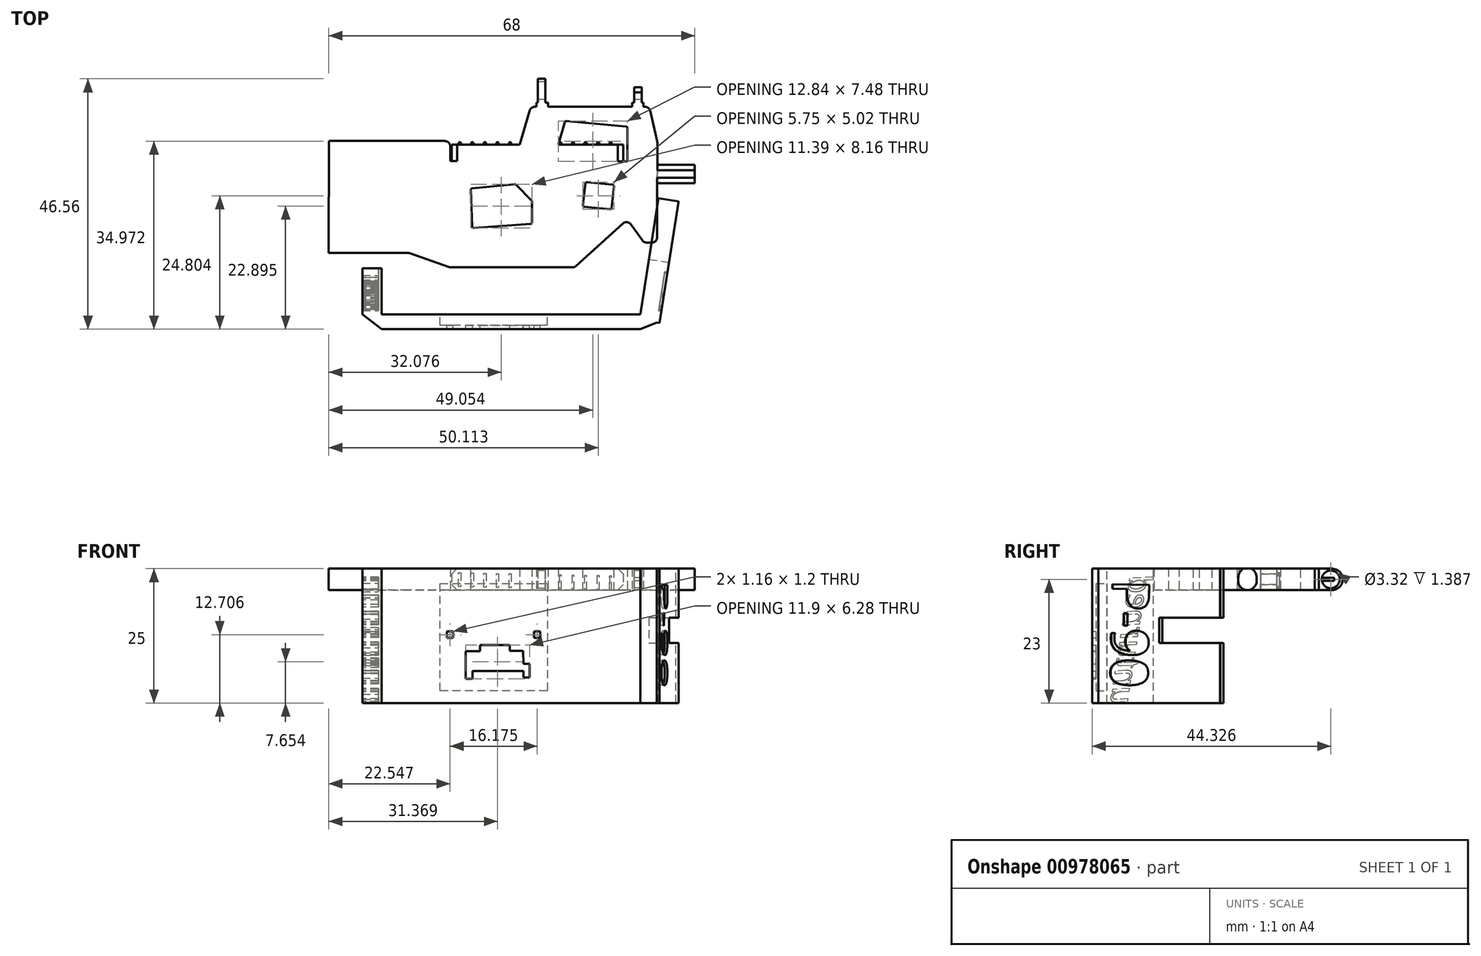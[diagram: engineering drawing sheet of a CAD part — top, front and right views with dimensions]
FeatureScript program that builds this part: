
annotation { "Feature Type Name" : "Feature", "Feature Type Description" : "" }
export const myFeature = defineFeature(function(context is Context, id is Id, definition is map)
    precondition{}
    {
        {
            var Q0;
            Q0=qCreatedBy(makeId("Top.planeOp"),FACE);
            var sketch = newSketch(context, id + "F0", { "sketchPlane" : qUnion([Q0])});
            skLineSegment(sketch, "E0", {"start": v(-19.87, -5.27) * mm, "end": v(2.7, -5.27) * mm});
            skLineSegment(sketch, "E1", {"start": v(2.7, -5.27) * mm, "end": v(2.7, -8.97) * mm});
            skLineSegment(sketch, "E2", {"start": v(2.7, -8.97) * mm, "end": v(14.76, -8.97) * mm});
            skLineSegment(sketch, "E3", {"start": v(14.76, -8.97) * mm, "end": v(17.64, 1.08) * mm});
            skLineSegment(sketch, "E4", {"start": v(17.64, 1.08) * mm, "end": v(18.71, 1.08) * mm});
            skLineSegment(sketch, "E5", {"start": v(18.71, 1.08) * mm, "end": v(18.71, 1.84) * mm});
            skLineSegment(sketch, "E6", {"start": v(18.71, 1.84) * mm, "end": v(18.98, 1.84) * mm});
            skLineSegment(sketch, "E7", {"start": v(18.98, 1.84) * mm, "end": v(18.98, 6.3) * mm});
            skLineSegment(sketch, "E8", {"start": v(18.98, 6.3) * mm, "end": v(20.34, 6.3) * mm});
            skLineSegment(sketch, "E9", {"start": v(20.34, 6.3) * mm, "end": v(20.37, 1.84) * mm});
            skLineSegment(sketch, "E10", {"start": v(20.37, 1.84) * mm, "end": v(20.86, 1.84) * mm});
            skLineSegment(sketch, "E11", {"start": v(20.86, 1.84) * mm, "end": v(20.86, 1.1) * mm});
            skLineSegment(sketch, "E12", {"start": v(20.86, 1.1) * mm, "end": v(36.46, 1.1) * mm});
            skLineSegment(sketch, "E13", {"start": v(36.46, 1.1) * mm, "end": v(36.46, 1.84) * mm});
            skLineSegment(sketch, "E14", {"start": v(36.46, 1.84) * mm, "end": v(36.87, 1.84) * mm});
            skLineSegment(sketch, "E15", {"start": v(36.87, 1.84) * mm, "end": v(36.87, 3.78) * mm});
            skLineSegment(sketch, "E16", {"start": v(36.87, 3.78) * mm, "end": v(38.25, 3.78) * mm});
            skLineSegment(sketch, "E17", {"start": v(38.25, 3.78) * mm, "end": v(38.25, 1.84) * mm});
            skLineSegment(sketch, "E18", {"start": v(38.25, 1.84) * mm, "end": v(38.6, 1.84) * mm});
            skLineSegment(sketch, "E19", {"start": v(38.6, 1.84) * mm, "end": v(38.6, 1.1) * mm});
            skLineSegment(sketch, "E20", {"start": v(38.6, 1.1) * mm, "end": v(39.64, 1.1) * mm});
            skLineSegment(sketch, "E21", {"start": v(39.64, 1.1) * mm, "end": v(41.15, -5.34) * mm});
            skLineSegment(sketch, "E22", {"start": v(41.15, -5.34) * mm, "end": v(41.15, -9.7) * mm});
            skLineSegment(sketch, "E23", {"start": v(41.15, -9.7) * mm, "end": v(48.11, -9.7) * mm});
            skLineSegment(sketch, "E24", {"start": v(48.11, -9.7) * mm, "end": v(48.11, -13.13) * mm});
            skLineSegment(sketch, "E25", {"start": v(48.11, -13.13) * mm, "end": v(41.14, -13.13) * mm});
            skLineSegment(sketch, "E26", {"start": v(41.14, -13.13) * mm, "end": v(41.14, -24.16) * mm});
            skLineSegment(sketch, "E27", {"start": v(41.14, -24.16) * mm, "end": v(38.66, -24.16) * mm});
            skLineSegment(sketch, "E28", {"start": v(38.66, -24.16) * mm, "end": v(35.58, -19.85) * mm});
            skLineSegment(sketch, "E29", {"start": v(35.58, -19.85) * mm, "end": v(25.77, -28.76) * mm});
            skLineSegment(sketch, "E30", {"start": v(25.77, -28.76) * mm, "end": v(2.57, -28.76) * mm});
            skLineSegment(sketch, "E31", {"start": v(2.57, -28.76) * mm, "end": v(-4.99, -26.08) * mm});
            skLineSegment(sketch, "E32", {"start": v(-4.99, -26.08) * mm, "end": v(-19.89, -26.08) * mm});
            skLineSegment(sketch, "E33", {"start": v(-19.89, -26.08) * mm, "end": v(-19.87, -5.27) * mm});
            skLineSegment(sketch, "E34", {"start": v(2.96, -5.97) * mm, "end": v(2.96, -8.97) * mm});
            skLineSegment(sketch, "E35", {"start": v(2.96, -5.97) * mm, "end": v(15.62, -5.97) * mm});
            skLineSegment(sketch, "E36", {"start": v(22.62, -5.96) * mm, "end": v(34.83, -5.96) * mm});
            skLineSegment(sketch, "E37", {"start": v(34.83, -5.96) * mm, "end": v(34.83, -9.03) * mm});
            skLineSegment(sketch, "E38", {"start": v(34.83, -9.03) * mm, "end": v(21.86, -9.03) * mm});
            skLineSegment(sketch, "E39", {"start": v(21.86, -9.03) * mm, "end": v(24.02, -1.53) * mm});
            skLineSegment(sketch, "E40", {"start": v(24.02, -1.53) * mm, "end": v(35.58, -2.57) * mm});
            skLineSegment(sketch, "E41", {"start": v(35.58, -2.57) * mm, "end": v(35.58, -9.03) * mm});
            skLineSegment(sketch, "E42", {"start": v(35.58, -9.03) * mm, "end": v(34.83, -9.03) * mm});
            skLineSegment(sketch, "E43", {"start": v(27.78, -12.92) * mm, "end": v(27.32, -17.45) * mm});
            skLineSegment(sketch, "E44", {"start": v(27.32, -17.45) * mm, "end": v(32.66, -18) * mm});
            skLineSegment(sketch, "E45", {"start": v(32.66, -18) * mm, "end": v(33.13, -13.41) * mm});
            skLineSegment(sketch, "E46", {"start": v(33.13, -13.41) * mm, "end": v(27.78, -12.92) * mm});
            skLineSegment(sketch, "E47", {"start": v(14.8, -13.27) * mm, "end": v(17.88, -16.43) * mm});
            skLineSegment(sketch, "E48", {"start": v(17.88, -16.43) * mm, "end": v(17.88, -20.66) * mm});
            skLineSegment(sketch, "E49", {"start": v(17.88, -20.66) * mm, "end": v(6.8, -21.47) * mm});
            skLineSegment(sketch, "E50", {"start": v(6.8, -21.47) * mm, "end": v(6.48, -14.11) * mm});
            skLineSegment(sketch, "E51", {"start": v(6.48, -14.11) * mm, "end": v(14.8, -13.27) * mm});
            skSolve(sketch);
        }
        {
            var Q0;
            Q0=makeQuery(id+"F0.imprint","IMPRINT",FACE,{"disambiguationData":[TD([[makeQuery(id+"F0.imprint","IMPRINT",EDGE,{"derivedFrom":sQuery(id+"F0.wireOp",EDGE,"E0")}),-1.0]])]});
            var Q1;
            {var subQ3=sQuery(id+"F0.wireOp",EDGE,"E34");Q1=makeQuery(id+"F0.imprint","IMPRINT",FACE,{"disambiguationData":[TD([[makeQuery(id+"F0.imprint","IMPRINT",EDGE,{"derivedFrom":subQ3}),1.0]])]});}
            var Q2;
            {var subQ0=sQuery(id+"F0.wireOp",EDGE,"E37");Q2=makeQuery(id+"F0.imprint","IMPRINT",FACE,{"disambiguationData":[TD([[makeQuery(id+"F0.imprint","IMPRINT",EDGE,{"derivedFrom":subQ0}),-1.0]])]});}
            extrude(context, id + "F1", {"entities" : qUnion([Q0, Q1, Q2]), "depth" : 4 * mm, "offsetDistance" : 25.4 * mm});
        }
        {
            var Q0;
            Q0=makeQuery(id+"F1.opExtrude","SWEPT_FACE",FACE,{"disambiguationData":[OSD([sQuery(id+"F0.wireOp",EDGE,"E7")])]});
            var sketch = newSketch(context, id + "F2", { "sketchPlane" : qUnion([Q0])});
            skLineSegment(sketch, "E52", {"start": v(-6.3, 0) * mm, "end": v(-1.84, 4) * mm});
            skLineSegment(sketch, "E53", {"start": v(-6.3, 4) * mm, "end": v(-1.84, 0) * mm});
            skCircle(sketch, "E54", {"center": v(-4.07, 2) * mm, "radius": 1.66 * mm});
            skSolve(sketch);
        }
        {
            var Q0;
            Q0 = qSketchRegion(id + "F2", true);
            extrude(context, id + "F3", {"entities" : qUnion([Q0]), "operationType" : NewBodyOperationType.REMOVE, "oppositeDirection" : true, "depth" : 25 * mm, "offsetDistance" : 25 * mm});
        }
        {
            var Q0;
            Q0=makeQuery(id+"F1.opExtrude","CAP_EDGE",EDGE,{"disambiguationData":[OSD([sQuery(id+"F0.wireOp",EDGE,"E23")])],"isStart":false});
            var Q1;
            Q1=makeQuery(id+"F1.opExtrude","CAP_EDGE",EDGE,{"disambiguationData":[OSD([sQuery(id+"F0.wireOp",EDGE,"E23")])],"isStart":true});
            var Q2;
            Q2=makeQuery(id+"F1.opExtrude","CAP_EDGE",EDGE,{"disambiguationData":[OSD([sQuery(id+"F0.wireOp",EDGE,"E25")])],"isStart":false});
            var Q3;
            Q3=makeQuery(id+"F1.opExtrude","CAP_EDGE",EDGE,{"disambiguationData":[OSD([sQuery(id+"F0.wireOp",EDGE,"E25")])],"isStart":true});
            fillet(context, id + "F4", {"entities" : qUnion([Q0, Q1, Q2, Q3]), "radius" : 1.7 * mm, "tangentPropagation" : true, "allowEdgeOverflow" : false});
        }
        {
            var Q0;
            Q0=makeQuery(id+"F1.opExtrude","CAP_EDGE",EDGE,{"disambiguationData":[OSD([sQuery(id+"F0.wireOp",EDGE,"E34")])],"isStart":false});
            var Q1;
            Q1=makeQuery(id+"F1.opExtrude","CAP_EDGE",EDGE,{"disambiguationData":[OSD([sQuery(id+"F0.wireOp",EDGE,"E34")])],"isStart":true});
            var Q2;
            Q2=makeQuery(id+"F1.opExtrude","CAP_EDGE",EDGE,{"disambiguationData":[OSD([sQuery(id+"F0.wireOp",EDGE,"E37")])],"isStart":false});
            var Q3;
            Q3=makeQuery(id+"F1.opExtrude","CAP_EDGE",EDGE,{"disambiguationData":[OSD([sQuery(id+"F0.wireOp",EDGE,"E37")])],"isStart":true});
            chamfer(context, id + "F5", {"entities" : qUnion([Q0, Q1, Q2, Q3]), "width" : 1 * mm, "tangentPropagation" : true});
        }
        {
            var Q0;
            Q0=makeQuery(id+"F1.opExtrude","CAP_FACE",FACE,{"disambiguationData":[OSD([sQuery(id+"F0.wireOp",EDGE,"E0"),sQuery(id+"F0.wireOp",EDGE,"E1"),sQuery(id+"F0.wireOp",EDGE,"E2"),sQuery(id+"F0.wireOp",EDGE,"E3"),sQuery(id+"F0.wireOp",EDGE,"E4"),sQuery(id+"F0.wireOp",EDGE,"E5"),sQuery(id+"F0.wireOp",EDGE,"E6"),sQuery(id+"F0.wireOp",EDGE,"E7"),sQuery(id+"F0.wireOp",EDGE,"E8"),sQuery(id+"F0.wireOp",EDGE,"E9"),sQuery(id+"F0.wireOp",EDGE,"E10"),sQuery(id+"F0.wireOp",EDGE,"E11"),sQuery(id+"F0.wireOp",EDGE,"E12"),sQuery(id+"F0.wireOp",EDGE,"E13"),sQuery(id+"F0.wireOp",EDGE,"E14"),sQuery(id+"F0.wireOp",EDGE,"E15"),sQuery(id+"F0.wireOp",EDGE,"E16"),sQuery(id+"F0.wireOp",EDGE,"E17"),sQuery(id+"F0.wireOp",EDGE,"E18"),sQuery(id+"F0.wireOp",EDGE,"E19"),sQuery(id+"F0.wireOp",EDGE,"E20"),sQuery(id+"F0.wireOp",EDGE,"E21"),sQuery(id+"F0.wireOp",EDGE,"E22"),sQuery(id+"F0.wireOp",EDGE,"E23"),sQuery(id+"F0.wireOp",EDGE,"E24"),sQuery(id+"F0.wireOp",EDGE,"E25"),sQuery(id+"F0.wireOp",EDGE,"E26"),sQuery(id+"F0.wireOp",EDGE,"E27"),sQuery(id+"F0.wireOp",EDGE,"E28"),sQuery(id+"F0.wireOp",EDGE,"E29"),sQuery(id+"F0.wireOp",EDGE,"E30"),sQuery(id+"F0.wireOp",EDGE,"E31"),sQuery(id+"F0.wireOp",EDGE,"E32"),sQuery(id+"F0.wireOp",EDGE,"E33"),sQuery(id+"F0.wireOp",EDGE,"E34"),sQuery(id+"F0.wireOp",EDGE,"E35"),sQuery(id+"F0.wireOp",EDGE,"E36"),sQuery(id+"F0.wireOp",EDGE,"E37"),sQuery(id+"F0.wireOp",EDGE,"E39"),sQuery(id+"F0.wireOp",EDGE,"E40"),sQuery(id+"F0.wireOp",EDGE,"E41"),sQuery(id+"F0.wireOp",EDGE,"E42"),sQuery(id+"F0.wireOp",EDGE,"E43"),sQuery(id+"F0.wireOp",EDGE,"E44"),sQuery(id+"F0.wireOp",EDGE,"E45"),sQuery(id+"F0.wireOp",EDGE,"E46"),sQuery(id+"F0.wireOp",EDGE,"E47"),sQuery(id+"F0.wireOp",EDGE,"E48"),sQuery(id+"F0.wireOp",EDGE,"E49"),sQuery(id+"F0.wireOp",EDGE,"E50"),sQuery(id+"F0.wireOp",EDGE,"E51")])],"isStart":false});
            var sketch = newSketch(context, id + "F6", { "sketchPlane" : qUnion([Q0])});
            skLineSegment(sketch, "E55", {"start": v(3.96, -8.97) * mm, "end": v(33.83, -9.03) * mm});
            skSolve(sketch);
        }
        {
            var Q0;
            Q0=makeQuery(id+"F1.opExtrude","SWEPT_EDGE",EDGE,{"disambiguationData":[OSD([sQuery(id+"F0.wireOp",EDGE,"E31"),sQuery(id+"F0.wireOp",EDGE,"E32")])]});
            var Q1;
            Q1=makeQuery(id+"F1.opExtrude","SWEPT_EDGE",EDGE,{"disambiguationData":[OSD([sQuery(id+"F0.wireOp",EDGE,"E30"),sQuery(id+"F0.wireOp",EDGE,"E31")])]});
            var Q2;
            Q2=makeQuery(id+"F1.opExtrude","SWEPT_EDGE",EDGE,{"disambiguationData":[OSD([sQuery(id+"F0.wireOp",EDGE,"E29"),sQuery(id+"F0.wireOp",EDGE,"E30")])]});
            var Q3;
            Q3=makeQuery(id+"F1.opExtrude","SWEPT_EDGE",EDGE,{"disambiguationData":[OSD([sQuery(id+"F0.wireOp",EDGE,"E28"),sQuery(id+"F0.wireOp",EDGE,"E29")])]});
            var Q4;
            Q4=makeQuery(id+"F1.opExtrude","SWEPT_EDGE",EDGE,{"disambiguationData":[OSD([sQuery(id+"F0.wireOp",EDGE,"E27"),sQuery(id+"F0.wireOp",EDGE,"E28")])]});
            var Q5;
            Q5=makeQuery(id+"F1.opExtrude","SWEPT_EDGE",EDGE,{"disambiguationData":[OSD([sQuery(id+"F0.wireOp",EDGE,"E26"),sQuery(id+"F0.wireOp",EDGE,"E27")])]});
            var Q6;
            Q6=makeQuery(id+"F1.opExtrude","SWEPT_EDGE",EDGE,{"disambiguationData":[OSD([sQuery(id+"F0.wireOp",EDGE,"E21"),sQuery(id+"F0.wireOp",EDGE,"E22")])]});
            var Q7;
            Q7=makeQuery(id+"F1.opExtrude","SWEPT_EDGE",EDGE,{"disambiguationData":[OSD([sQuery(id+"F0.wireOp",EDGE,"E20"),sQuery(id+"F0.wireOp",EDGE,"E21")])]});
            var Q8;
            Q8=makeQuery(id+"F1.opExtrude","SWEPT_EDGE",EDGE,{"disambiguationData":[OSD([sQuery(id+"F0.wireOp",EDGE,"E3"),sQuery(id+"F0.wireOp",EDGE,"E4")])]});
            var Q9;
            Q9=makeQuery(id+"F1.opExtrude","SWEPT_EDGE",EDGE,{"disambiguationData":[OSD([sQuery(id+"F0.wireOp",EDGE,"E0"),sQuery(id+"F0.wireOp",EDGE,"E1")])]});
            fillet(context, id + "F7", {"entities" : qUnion([Q0, Q1, Q2, Q3, Q4, Q5, Q6, Q7, Q8, Q9]), "radius" : 1 * mm, "tangentPropagation" : true, "allowEdgeOverflow" : false});
        }
        {
            var Q0;
            Q0=makeQuery(id+"F1.opExtrude","SWEPT_FACE",FACE,{"disambiguationData":[OSD([sQuery(id+"F0.wireOp",EDGE,"E35")])]});
            var sketch = newSketch(context, id + "F8", { "sketchPlane" : qUnion([Q0])});
            skLineSegment(sketch, "E56", {"start": v(-4.25, 0.64) * mm, "end": v(-4.25, 3.24) * mm});
            skLineSegment(sketch, "E57", {"start": v(-4.25, 3.24) * mm, "end": v(-4.66, 3.24) * mm});
            skLineSegment(sketch, "E58", {"start": v(-4.66, 3.24) * mm, "end": v(-4.66, 0.65) * mm});
            skLineSegment(sketch, "E59", {"start": v(-4.66, 0.65) * mm, "end": v(-4.25, 0.64) * mm});
            skLineSegment(sketch, "E60.1.0.0", {"start": v(-6.59, 0.59) * mm, "end": v(-6.59, 3.2) * mm});
            skLineSegment(sketch, "E60.1.0.1", {"start": v(-7, 3.2) * mm, "end": v(-7, 0.6) * mm});
            skLineSegment(sketch, "E60.1.0.2", {"start": v(-7, 0.6) * mm, "end": v(-6.59, 0.59) * mm});
            skLineSegment(sketch, "E60.1.0.3", {"start": v(-6.59, 3.2) * mm, "end": v(-7, 3.2) * mm});
            skLineSegment(sketch, "E60.2.0.0", {"start": v(-8.92, 0.53) * mm, "end": v(-8.92, 3.14) * mm});
            skLineSegment(sketch, "E60.2.0.1", {"start": v(-9.34, 3.14) * mm, "end": v(-9.34, 0.55) * mm});
            skLineSegment(sketch, "E60.2.0.2", {"start": v(-9.34, 0.55) * mm, "end": v(-8.92, 0.53) * mm});
            skLineSegment(sketch, "E60.2.0.3", {"start": v(-8.92, 3.14) * mm, "end": v(-9.34, 3.14) * mm});
            skLineSegment(sketch, "E60.3.0.0", {"start": v(-11.26, 0.48) * mm, "end": v(-11.26, 3.08) * mm});
            skLineSegment(sketch, "E60.3.0.1", {"start": v(-11.67, 3.08) * mm, "end": v(-11.67, 0.5) * mm});
            skLineSegment(sketch, "E60.3.0.2", {"start": v(-11.67, 0.5) * mm, "end": v(-11.26, 0.48) * mm});
            skLineSegment(sketch, "E60.3.0.3", {"start": v(-11.26, 3.08) * mm, "end": v(-11.67, 3.08) * mm});
            skLineSegment(sketch, "E60.4.0.0", {"start": v(-13.6, 0.43) * mm, "end": v(-13.6, 3.03) * mm});
            skLineSegment(sketch, "E60.4.0.1", {"start": v(-14, 3.03) * mm, "end": v(-14, 0.44) * mm});
            skLineSegment(sketch, "E60.4.0.2", {"start": v(-14, 0.44) * mm, "end": v(-13.6, 0.43) * mm});
            skLineSegment(sketch, "E60.4.0.3", {"start": v(-13.6, 3.03) * mm, "end": v(-14, 3.03) * mm});
            skLineSegment(sketch, "E60.direction1", {"start": v(-4.66, 0.65) * mm, "end": v(-7, 0.6) * mm, "construction": true});
            skLineSegment(sketch, "E61.0.5.0", {"start": v(-15.93, 0.37) * mm, "end": v(-15.93, 2.98) * mm});
            skLineSegment(sketch, "E61.3.5.0", {"start": v(-16.35, 2.98) * mm, "end": v(-16.35, 0.39) * mm});
            skLineSegment(sketch, "E61.6.5.0", {"start": v(-16.35, 0.39) * mm, "end": v(-15.93, 0.37) * mm});
            skLineSegment(sketch, "E61.9.5.0", {"start": v(-15.93, 2.98) * mm, "end": v(-16.35, 2.98) * mm});
            skLineSegment(sketch, "E61.0.6.0", {"start": v(-18.27, 0.32) * mm, "end": v(-18.27, 2.92) * mm});
            skLineSegment(sketch, "E61.3.6.0", {"start": v(-18.68, 2.92) * mm, "end": v(-18.68, 0.33) * mm});
            skLineSegment(sketch, "E61.6.6.0", {"start": v(-18.68, 0.33) * mm, "end": v(-18.27, 0.32) * mm});
            skLineSegment(sketch, "E61.9.6.0", {"start": v(-18.27, 2.92) * mm, "end": v(-18.68, 2.92) * mm});
            skLineSegment(sketch, "E61.0.7.0", {"start": v(-20.6, 0.27) * mm, "end": v(-20.6, 2.87) * mm});
            skLineSegment(sketch, "E61.3.7.0", {"start": v(-21.02, 2.87) * mm, "end": v(-21.02, 0.28) * mm});
            skLineSegment(sketch, "E61.6.7.0", {"start": v(-21.02, 0.28) * mm, "end": v(-20.6, 0.27) * mm});
            skLineSegment(sketch, "E61.9.7.0", {"start": v(-20.6, 2.87) * mm, "end": v(-21.02, 2.87) * mm});
            skLineSegment(sketch, "E61.0.8.0", {"start": v(-22.94, 0.21) * mm, "end": v(-22.94, 2.82) * mm});
            skLineSegment(sketch, "E61.3.8.0", {"start": v(-23.36, 2.82) * mm, "end": v(-23.36, 0.23) * mm});
            skLineSegment(sketch, "E61.6.8.0", {"start": v(-23.36, 0.23) * mm, "end": v(-22.94, 0.21) * mm});
            skLineSegment(sketch, "E61.9.8.0", {"start": v(-22.94, 2.82) * mm, "end": v(-23.36, 2.82) * mm});
            skLineSegment(sketch, "E61.0.9.0", {"start": v(-25.28, 0.16) * mm, "end": v(-25.28, 2.76) * mm});
            skLineSegment(sketch, "E61.3.9.0", {"start": v(-25.7, 2.76) * mm, "end": v(-25.7, 0.17) * mm});
            skLineSegment(sketch, "E61.6.9.0", {"start": v(-25.7, 0.17) * mm, "end": v(-25.28, 0.16) * mm});
            skLineSegment(sketch, "E61.9.9.0", {"start": v(-25.28, 2.76) * mm, "end": v(-25.7, 2.76) * mm});
            skLineSegment(sketch, "E61.0.10.0", {"start": v(-27.62, 0.1) * mm, "end": v(-27.62, 2.71) * mm});
            skLineSegment(sketch, "E61.3.10.0", {"start": v(-28.03, 2.71) * mm, "end": v(-28.03, 0.12) * mm});
            skLineSegment(sketch, "E61.6.10.0", {"start": v(-28.03, 0.12) * mm, "end": v(-27.62, 0.1) * mm});
            skLineSegment(sketch, "E61.9.10.0", {"start": v(-27.62, 2.71) * mm, "end": v(-28.03, 2.71) * mm});
            skLineSegment(sketch, "E61.0.11.0", {"start": v(-29.95, 0.05) * mm, "end": v(-29.95, 2.66) * mm});
            skLineSegment(sketch, "E61.3.11.0", {"start": v(-30.37, 2.66) * mm, "end": v(-30.37, 0.07) * mm});
            skLineSegment(sketch, "E61.6.11.0", {"start": v(-30.37, 0.07) * mm, "end": v(-29.95, 0.05) * mm});
            skLineSegment(sketch, "E61.9.11.0", {"start": v(-29.95, 2.66) * mm, "end": v(-30.37, 2.66) * mm});
            skLineSegment(sketch, "E61.0.12.0", {"start": v(-32.29, 0) * mm, "end": v(-32.29, 2.6) * mm});
            skLineSegment(sketch, "E61.3.12.0", {"start": v(-32.7, 2.6) * mm, "end": v(-32.7, 0.01) * mm});
            skLineSegment(sketch, "E61.6.12.0", {"start": v(-32.7, 0.01) * mm, "end": v(-32.29, 0) * mm});
            skLineSegment(sketch, "E61.9.12.0", {"start": v(-32.29, 2.6) * mm, "end": v(-32.7, 2.6) * mm});
            skSolve(sketch);
        }
        {
            var Q0;
            Q0 = qSketchRegion(id + "F8", true);
            extrude(context, id + "F9", {"entities" : qUnion([Q0]), "operationType" : NewBodyOperationType.ADD, "depth" : .5 * mm, "offsetDistance" : 25 * mm});
        }
        {
            var Q0;
            Q0=makeQuery(id+"F9.opExtrude","CAP_EDGE",EDGE,{"disambiguationData":[OSD([sQuery(id+"F8.wireOp",EDGE,"E56")])],"isStart":false});
            var Q1;
            Q1=makeQuery(id+"F9.opExtrude","CAP_EDGE",EDGE,{"disambiguationData":[OSD([sQuery(id+"F8.wireOp",EDGE,"E58")])],"isStart":false});
            var Q2;
            Q2=makeQuery(id+"F9.opExtrude","CAP_EDGE",EDGE,{"disambiguationData":[OSD([sQuery(id+"F8.wireOp",EDGE,"E60.1.0.0")])],"isStart":false});
            var Q3;
            Q3=makeQuery(id+"F9.opExtrude","CAP_EDGE",EDGE,{"disambiguationData":[OSD([sQuery(id+"F8.wireOp",EDGE,"E60.1.0.1")])],"isStart":false});
            var Q4;
            Q4=makeQuery(id+"F9.opExtrude","CAP_EDGE",EDGE,{"disambiguationData":[OSD([sQuery(id+"F8.wireOp",EDGE,"E60.2.0.0")])],"isStart":false});
            var Q5;
            Q5=makeQuery(id+"F9.opExtrude","CAP_EDGE",EDGE,{"disambiguationData":[OSD([sQuery(id+"F8.wireOp",EDGE,"E60.2.0.1")])],"isStart":false});
            var Q6;
            Q6=makeQuery(id+"F9.opExtrude","CAP_EDGE",EDGE,{"disambiguationData":[OSD([sQuery(id+"F8.wireOp",EDGE,"E60.3.0.0")])],"isStart":false});
            var Q7;
            Q7=makeQuery(id+"F9.opExtrude","CAP_EDGE",EDGE,{"disambiguationData":[OSD([sQuery(id+"F8.wireOp",EDGE,"E60.3.0.1")])],"isStart":false});
            var Q8;
            Q8=makeQuery(id+"F9.opExtrude","CAP_EDGE",EDGE,{"disambiguationData":[OSD([sQuery(id+"F8.wireOp",EDGE,"E60.4.0.0")])],"isStart":false});
            var Q9;
            Q9=makeQuery(id+"F9.opExtrude","CAP_EDGE",EDGE,{"disambiguationData":[OSD([sQuery(id+"F8.wireOp",EDGE,"E60.4.0.1")])],"isStart":false});
            var Q10;
            Q10=makeQuery(id+"F9.opExtrude","CAP_EDGE",EDGE,{"disambiguationData":[OSD([sQuery(id+"F8.wireOp",EDGE,"E61.3.8.0")])],"isStart":false});
            var Q11;
            Q11=makeQuery(id+"F9.opExtrude","CAP_EDGE",EDGE,{"disambiguationData":[OSD([sQuery(id+"F8.wireOp",EDGE,"E61.0.8.0")])],"isStart":false});
            var Q12;
            Q12=makeQuery(id+"F9.opExtrude","CAP_EDGE",EDGE,{"disambiguationData":[OSD([sQuery(id+"F8.wireOp",EDGE,"E61.3.9.0")])],"isStart":false});
            var Q13;
            Q13=makeQuery(id+"F9.opExtrude","CAP_EDGE",EDGE,{"disambiguationData":[OSD([sQuery(id+"F8.wireOp",EDGE,"E61.0.9.0")])],"isStart":false});
            var Q14;
            Q14=makeQuery(id+"F9.opExtrude","CAP_EDGE",EDGE,{"disambiguationData":[OSD([sQuery(id+"F8.wireOp",EDGE,"E61.0.10.0")])],"isStart":false});
            var Q15;
            Q15=makeQuery(id+"F9.opExtrude","CAP_EDGE",EDGE,{"disambiguationData":[OSD([sQuery(id+"F8.wireOp",EDGE,"E61.3.10.0")])],"isStart":false});
            var Q16;
            Q16=makeQuery(id+"F9.opExtrude","CAP_EDGE",EDGE,{"disambiguationData":[OSD([sQuery(id+"F8.wireOp",EDGE,"E61.0.11.0")])],"isStart":false});
            var Q17;
            Q17=makeQuery(id+"F9.opExtrude","CAP_EDGE",EDGE,{"disambiguationData":[OSD([sQuery(id+"F8.wireOp",EDGE,"E61.3.11.0")])],"isStart":false});
            var Q18;
            Q18=makeQuery(id+"F9.opExtrude","CAP_EDGE",EDGE,{"disambiguationData":[OSD([sQuery(id+"F8.wireOp",EDGE,"E61.0.12.0")])],"isStart":false});
            var Q19;
            Q19=makeQuery(id+"F9.opExtrude","CAP_EDGE",EDGE,{"disambiguationData":[OSD([sQuery(id+"F8.wireOp",EDGE,"E61.3.12.0")])],"isStart":false});
            fillet(context, id + "F10", {"entities" : qUnion([Q0, Q1, Q2, Q3, Q4, Q5, Q6, Q7, Q8, Q9, Q10, Q11, Q12, Q13, Q14, Q15, Q16, Q17, Q18, Q19]), "radius" : .2 * mm, "tangentPropagation" : true, "allowEdgeOverflow" : false});
        }
        {
            var Q0;
            {var subQ50=sQuery(id+"F0.wireOp",EDGE,"E0");Q0=makeQuery(id+"F6.imprint","IMPRINT",FACE,{"disambiguationData":[TD([[makeQuery(id+"F6.imprint","IMPRINT",EDGE,{"derivedFrom":makeQuery(id+"F1.opExtrude","CAP_EDGE",EDGE,{"disambiguationData":[OSD([subQ50])],"isStart":false})}),-1.0]])]});}
            var sketch = newSketch(context, id + "F11", { "sketchPlane" : qUnion([Q0])});
            skLineSegment(sketch, "E62", {"start": v(41.38, -15.9) * mm, "end": v(38.02, -37.53) * mm});
            skLineSegment(sketch, "E63", {"start": v(38.02, -37.53) * mm, "end": v(-10.06, -37.53) * mm});
            skLineSegment(sketch, "E64", {"start": v(-10.06, -37.53) * mm, "end": v(-10.06, -28.9) * mm});
            skLineSegment(sketch, "E65", {"start": v(-10.06, -28.9) * mm, "end": v(-13.64, -28.9) * mm});
            skLineSegment(sketch, "E66", {"start": v(-13.64, -28.9) * mm, "end": v(-13.64, -37.53) * mm});
            skLineSegment(sketch, "E67", {"start": v(-13.64, -37.53) * mm, "end": v(-10.06, -40.26) * mm});
            skLineSegment(sketch, "E68", {"start": v(-10.06, -40.26) * mm, "end": v(38.02, -40.26) * mm});
            skLineSegment(sketch, "E69", {"start": v(38.02, -40.26) * mm, "end": v(41.08, -39.04) * mm});
            skLineSegment(sketch, "E70", {"start": v(41.08, -39.04) * mm, "end": v(44.58, -16.43) * mm});
            skLineSegment(sketch, "E71", {"start": v(41.38, -15.9) * mm, "end": v(44.58, -16.43) * mm});
            skSolve(sketch);
        }
        {
            var Q0;
            Q0 = qSketchRegion(id + "F11", true);
            extrude(context, id + "F12", {"entities" : qUnion([Q0]), "oppositeDirection" : true, "depth" : 25 * mm, "offsetDistance" : 25 * mm});
        }
        {
            var Q0;
            Q0=makeQuery(id+"F12.opExtrude","SWEPT_FACE",FACE,{"disambiguationData":[OSD([sQuery(id+"F11.wireOp",EDGE,"E70")])]});
            var sketch = newSketch(context, id + "F13", { "sketchPlane" : qUnion([Q0])});
            skLineSegment(sketch, "E72", {"start": v(-9.4, -5.14) * mm, "end": v(-16.6, -5.14) * mm});
            skLineSegment(sketch, "E73", {"start": v(-16.6, -5.14) * mm, "end": v(-16.6, -9.85) * mm});
            skLineSegment(sketch, "E74", {"start": v(-16.6, -9.85) * mm, "end": v(-9.4, -9.85) * mm});
            skLineSegment(sketch, "E75", {"start": v(-16.6, -9.85) * mm, "end": v(-20.87, -9.85) * mm});
            skLineSegment(sketch, "E76", {"start": v(-20.87, -9.85) * mm, "end": v(-20.87, -5.14) * mm});
            skLineSegment(sketch, "E77", {"start": v(-20.87, -5.14) * mm, "end": v(-16.6, -5.14) * mm});
            skLineSegment(sketch, "E78", {"start": v(-9.4, -5.14) * mm, "end": v(-7.2, -5.14) * mm});
            skLineSegment(sketch, "E79", {"start": v(-7.2, -10.23) * mm, "end": v(-9.4, -9.85) * mm});
            skLineSegment(sketch, "E80", {"start": v(-7.2, -10.23) * mm, "end": v(-7.2, -5.14) * mm});
            skSolve(sketch);
        }
        {
            var Q0;
            Q0 = qSketchRegion(id + "F13", true);
            var Q1;
            {var subQ0=sQuery(id+"F13.wireOp",EDGE,"E72");Q1=makeQuery(id+"F13.imprint","IMPRINT",FACE,{"disambiguationData":[TD([[makeQuery(id+"F13.imprint","IMPRINT",EDGE,{"derivedFrom":subQ0}),1.0]])]});}
            extrude(context, id + "F14", {"entities" : qUnion([Q0, Q1]), "operationType" : NewBodyOperationType.REMOVE, "oppositeDirection" : true, "depth" : 4 * mm, "offsetDistance" : 25 * mm});
        }
        {
            var Q0;
            Q0=makeQuery(id+"F1.opExtrude","SWEPT_FACE",FACE,{"disambiguationData":[OSD([sQuery(id+"F0.wireOp",EDGE,"E15")])]});
            var sketch = newSketch(context, id + "F15", { "sketchPlane" : qUnion([Q0])});
            skLineSegment(sketch, "E81", {"start": v(-2.4, 2) * mm, "end": v(-4.7, 2) * mm});
            skLineSegment(sketch, "E82", {"start": v(-4.7, 2.3) * mm, "end": v(-2.43, 2.3) * mm});
            skLineSegment(sketch, "E83.MirrorCS", {"start": v(-4.7, 1.7) * mm, "end": v(-2.43, 1.7) * mm});
            skLineSegment(sketch, "E84", {"start": v(-4.7, 1.7) * mm, "end": v(-4.7, 2.3) * mm});
            skSolve(sketch);
        }
        {
            var Q0;
            {var subQ0=sQuery(id+"F15.wireOp",EDGE,"E81");Q0=makeQuery(id+"F15.imprint","IMPRINT",FACE,{"disambiguationData":[TD([[makeQuery(id+"F15.imprint","IMPRINT",EDGE,{"derivedFrom":subQ0}),1.0]])]});}
            var Q1;
            {var subQ0=sQuery(id+"F15.wireOp",EDGE,"E81");Q1=makeQuery(id+"F15.imprint","IMPRINT",FACE,{"disambiguationData":[TD([[makeQuery(id+"F15.imprint","IMPRINT",EDGE,{"derivedFrom":subQ0}),-1.0]])]});}
            extrude(context, id + "F16", {"entities" : qUnion([Q0, Q1]), "operationType" : NewBodyOperationType.ADD, "oppositeDirection" : true, "depth" : 1.4 * mm, "offsetDistance" : 25.4 * mm});
        }
        {
            var Q0;
            Q0=makeQuery(id+"F1.opExtrude","CAP_EDGE",EDGE,{"disambiguationData":[OSD([sQuery(id+"F0.wireOp",EDGE,"E8")])],"isStart":true});
            var Q1;
            Q1=makeQuery(id+"F1.opExtrude","CAP_EDGE",EDGE,{"disambiguationData":[OSD([sQuery(id+"F0.wireOp",EDGE,"E8")])],"isStart":false});
            fillet(context, id + "F17", {"entities" : qUnion([Q0, Q1]), "radius" : 2 * mm, "tangentPropagation" : true, "allowEdgeOverflow" : false});
        }
        {
            var Q0;
            Q0=makeQuery(id+"F1.opExtrude","CAP_EDGE",EDGE,{"disambiguationData":[OSD([sQuery(id+"F0.wireOp",EDGE,"E16")])],"isStart":false});
            var Q1;
            Q1=makeQuery(id+"F1.opExtrude","CAP_EDGE",EDGE,{"disambiguationData":[OSD([sQuery(id+"F0.wireOp",EDGE,"E16")])],"isStart":true});
            fillet(context, id + "F18", {"entities" : qUnion([Q0, Q1]), "radius" : 1 * mm, "tangentPropagation" : true, "allowEdgeOverflow" : false});
        }
        {
            var Q0;
            Q0=makeQuery(id+"F1.opExtrude","SWEPT_EDGE",EDGE,{"disambiguationData":[OSD([sQuery(id+"F0.wireOp",EDGE,"E39"),sQuery(id+"F0.wireOp",EDGE,"E40")])]});
            var Q1;
            Q1=makeQuery(id+"F1.opExtrude","SWEPT_EDGE",EDGE,{"disambiguationData":[OSD([sQuery(id+"F0.wireOp",EDGE,"E40"),sQuery(id+"F0.wireOp",EDGE,"E41")])]});
            var Q2;
            Q2=makeQuery(id+"F1.opExtrude","SWEPT_EDGE",EDGE,{"disambiguationData":[OSD([sQuery(id+"F0.wireOp",EDGE,"E45"),sQuery(id+"F0.wireOp",EDGE,"E46")])]});
            var Q3;
            Q3=makeQuery(id+"F1.opExtrude","SWEPT_EDGE",EDGE,{"disambiguationData":[OSD([sQuery(id+"F0.wireOp",EDGE,"E44"),sQuery(id+"F0.wireOp",EDGE,"E45")])]});
            var Q4;
            Q4=makeQuery(id+"F1.opExtrude","SWEPT_EDGE",EDGE,{"disambiguationData":[OSD([sQuery(id+"F0.wireOp",EDGE,"E43"),sQuery(id+"F0.wireOp",EDGE,"E44")])]});
            var Q5;
            Q5=makeQuery(id+"F1.opExtrude","SWEPT_EDGE",EDGE,{"disambiguationData":[OSD([sQuery(id+"F0.wireOp",EDGE,"E43"),sQuery(id+"F0.wireOp",EDGE,"E46")])]});
            var Q6;
            Q6=makeQuery(id+"F1.opExtrude","SWEPT_EDGE",EDGE,{"disambiguationData":[OSD([sQuery(id+"F0.wireOp",EDGE,"E47"),sQuery(id+"F0.wireOp",EDGE,"E48")])]});
            var Q7;
            Q7=makeQuery(id+"F1.opExtrude","SWEPT_EDGE",EDGE,{"disambiguationData":[OSD([sQuery(id+"F0.wireOp",EDGE,"E48"),sQuery(id+"F0.wireOp",EDGE,"E49")])]});
            var Q8;
            Q8=makeQuery(id+"F1.opExtrude","SWEPT_EDGE",EDGE,{"disambiguationData":[OSD([sQuery(id+"F0.wireOp",EDGE,"E47"),sQuery(id+"F0.wireOp",EDGE,"E51")])]});
            var Q9;
            Q9=makeQuery(id+"F1.opExtrude","SWEPT_EDGE",EDGE,{"disambiguationData":[OSD([sQuery(id+"F0.wireOp",EDGE,"E50"),sQuery(id+"F0.wireOp",EDGE,"E51")])]});
            var Q10;
            Q10=makeQuery(id+"F1.opExtrude","SWEPT_EDGE",EDGE,{"disambiguationData":[OSD([sQuery(id+"F0.wireOp",EDGE,"E49"),sQuery(id+"F0.wireOp",EDGE,"E50")])]});
            fillet(context, id + "F19", {"entities" : qUnion([Q0, Q1, Q2, Q3, Q4, Q5, Q6, Q7, Q8, Q9, Q10]), "radius" : .3 * mm, "tangentPropagation" : true, "allowEdgeOverflow" : false});
        }
        {
            var Q0;
            Q0=makeQuery(id+"F12.opExtrude","SWEPT_FACE",FACE,{"disambiguationData":[OSD([sQuery(id+"F11.wireOp",EDGE,"E63")])]});
            var sketch = newSketch(context, id + "F20", { "sketchPlane" : qUnion([Q0])});
            skLineSegment(sketch, "E85", {"start": v(-20.7, 1.23) * mm, "end": v(-20.7, -18.7) * mm});
            skLineSegment(sketch, "E86", {"start": v(-20.7, -18.7) * mm, "end": v(-0.78, -18.7) * mm});
            skLineSegment(sketch, "E87", {"start": v(-0.78, -18.7) * mm, "end": v(-0.78, 1.23) * mm});
            skLineSegment(sketch, "E88", {"start": v(-0.78, 1.23) * mm, "end": v(-20.7, 1.23) * mm});
            skLineSegment(sketch, "E89", {"start": v(-10.74, 1.23) * mm, "end": v(-10.74, -18.7) * mm});
            skLineSegment(sketch, "E90", {"start": v(-19.4, -7.7) * mm, "end": v(-18.25, -7.7) * mm});
            skLineSegment(sketch, "E91", {"start": v(-18.25, -7.7) * mm, "end": v(-18.25, -8.9) * mm});
            skLineSegment(sketch, "E92", {"start": v(-18.25, -8.9) * mm, "end": v(-19.4, -8.9) * mm});
            skLineSegment(sketch, "E93", {"start": v(-19.4, -8.9) * mm, "end": v(-19.4, -7.7) * mm});
            skLineSegment(sketch, "E94.MirrorCS", {"start": v(-3.23, -7.7) * mm, "end": v(-3.23, -8.9) * mm});
            skLineSegment(sketch, "E95.MirrorCS", {"start": v(-2.08, -7.7) * mm, "end": v(-3.23, -7.7) * mm});
            skLineSegment(sketch, "E96.MirrorCS", {"start": v(-2.09, -8.9) * mm, "end": v(-2.08, -7.7) * mm});
            skLineSegment(sketch, "E97.MirrorCS", {"start": v(-3.23, -8.9) * mm, "end": v(-2.09, -8.9) * mm});
            skLineSegment(sketch, "E98", {"start": v(-13.75, -11.28) * mm, "end": v(-16.21, -11.28) * mm});
            skLineSegment(sketch, "E99", {"start": v(-16.21, -11.28) * mm, "end": v(-16.29, -13.7) * mm});
            skLineSegment(sketch, "E100", {"start": v(-16.29, -13.7) * mm, "end": v(-17.4, -13.7) * mm});
            skLineSegment(sketch, "E101", {"start": v(-17.4, -13.7) * mm, "end": v(-17.43, -16.25) * mm});
            skLineSegment(sketch, "E102", {"start": v(-17.43, -16.25) * mm, "end": v(-16.27, -16.26) * mm});
            skLineSegment(sketch, "E103", {"start": v(-16.27, -16.26) * mm, "end": v(-16.26, -15.06) * mm});
            skLineSegment(sketch, "E104", {"start": v(-16.26, -15.06) * mm, "end": v(-6.84, -15.06) * mm});
            skLineSegment(sketch, "E105", {"start": v(-6.84, -15.06) * mm, "end": v(-6.84, -16.49) * mm});
            skLineSegment(sketch, "E106", {"start": v(-6.84, -16.49) * mm, "end": v(-5.53, -16.49) * mm});
            skLineSegment(sketch, "E107", {"start": v(-5.53, -16.49) * mm, "end": v(-5.53, -11.35) * mm});
            skLineSegment(sketch, "E108", {"start": v(-5.53, -11.35) * mm, "end": v(-8.25, -11.35) * mm});
            skLineSegment(sketch, "E109", {"start": v(-8.25, -11.35) * mm, "end": v(-8.23, -10.2) * mm});
            skLineSegment(sketch, "E110", {"start": v(-8.23, -10.2) * mm, "end": v(-13.72, -10.2) * mm});
            skLineSegment(sketch, "E111", {"start": v(-13.72, -10.2) * mm, "end": v(-13.75, -11.28) * mm});
            skSolve(sketch);
        }
        {
            var Q0;
            Q0=makeQuery(id+"F20.imprint","IMPRINT",FACE,{"disambiguationData":[TD([[makeQuery(id+"F20.imprint","IMPRINT",EDGE,{"derivedFrom":sQuery(id+"F20.wireOp",EDGE,"E98")}),1.0]])]});
            var Q1;
            {var subQ0=sQuery(id+"F20.wireOp",EDGE,"E105");Q1=makeQuery(id+"F20.imprint","IMPRINT",FACE,{"disambiguationData":[TD([[makeQuery(id+"F20.imprint","IMPRINT",EDGE,{"derivedFrom":subQ0}),1.0]])]});}
            var Q2;
            Q2=makeQuery(id+"F20.imprint","IMPRINT",FACE,{"disambiguationData":[TD([[makeQuery(id+"F20.imprint","IMPRINT",EDGE,{"derivedFrom":sQuery(id+"F20.wireOp",EDGE,"E90")}),-1.0]])]});
            var Q3;
            Q3=makeQuery(id+"F20.imprint","IMPRINT",FACE,{"disambiguationData":[TD([[makeQuery(id+"F20.imprint","IMPRINT",EDGE,{"derivedFrom":sQuery(id+"F20.wireOp",EDGE,"E94.MirrorCS")}),1.0]])]});
            extrude(context, id + "F21", {"entities" : qUnion([Q0, Q1, Q2, Q3]), "operationType" : NewBodyOperationType.REMOVE, "oppositeDirection" : true, "depth" : 5 * mm, "offsetDistance" : 25 * mm});
        }
        {
            var Q0;
            {var subQ6=sQuery(id+"F20.wireOp",EDGE,"E87");Q0=makeQuery(id+"F20.imprint","IMPRINT",FACE,{"disambiguationData":[TD([[makeQuery(id+"F20.imprint","IMPRINT",EDGE,{"derivedFrom":subQ6}),1.0]])]});}
            var Q1;
            {var subQ8=sQuery(id+"F20.wireOp",EDGE,"E85");Q1=makeQuery(id+"F20.imprint","IMPRINT",FACE,{"disambiguationData":[TD([[makeQuery(id+"F20.imprint","IMPRINT",EDGE,{"derivedFrom":subQ8}),1.0]])]});}
            extrude(context, id + "F22", {"entities" : qUnion([Q0, Q1]), "operationType" : NewBodyOperationType.REMOVE, "oppositeDirection" : true, "depth" : 2 * mm, "offsetDistance" : 25 * mm});
        }
        {
            var Q0;
            Q0=makeQuery(id+"F12.opExtrude","SWEPT_FACE",FACE,{"disambiguationData":[OSD([sQuery(id+"F11.wireOp",EDGE,"E66")])]});
            var sketch = newSketch(context, id + "F23", { "sketchPlane" : qUnion([Q0])});
            skText(sketch, "E112", { "text": "unturned", "fontName": "OpenSans-Italic.ttf"});
            const initialGuessF23  = {"E112": [0.03693, -0.021, -0.15335, 0.98817, 0.00427]};
            skSetInitialGuess(sketch, initialGuessF23);
            skSolve(sketch);
        }
        {
            var Q0;
            Q0=makeQuery(id+"F23.imprint","IMPRINT",FACE,{"disambiguationData":[TD([[makeQuery(id+"F23.imprint","IMPRINT",EDGE,{"derivedFrom":sQuery(id+"F23.wireOp",EDGE,"E112.sketch_text.stroke-0")}),-1.0]])]});
            var Q1;
            Q1=makeQuery(id+"F23.imprint","IMPRINT",FACE,{"disambiguationData":[TD([[makeQuery(id+"F23.imprint","IMPRINT",EDGE,{"derivedFrom":sQuery(id+"F23.wireOp",EDGE,"E112.sketch_text.stroke-19")}),-1.0]])]});
            var Q2;
            Q2=makeQuery(id+"F23.imprint","IMPRINT",FACE,{"disambiguationData":[TD([[makeQuery(id+"F23.imprint","IMPRINT",EDGE,{"derivedFrom":sQuery(id+"F23.wireOp",EDGE,"E112.sketch_text.stroke-39")}),-1.0]])]});
            var Q3;
            Q3=makeQuery(id+"F23.imprint","IMPRINT",FACE,{"disambiguationData":[TD([[makeQuery(id+"F23.imprint","IMPRINT",EDGE,{"derivedFrom":sQuery(id+"F23.wireOp",EDGE,"E112.sketch_text.stroke-60")}),-1.0]])]});
            var Q4;
            Q4=makeQuery(id+"F23.imprint","IMPRINT",FACE,{"disambiguationData":[TD([[makeQuery(id+"F23.imprint","IMPRINT",EDGE,{"derivedFrom":sQuery(id+"F23.wireOp",EDGE,"E112.sketch_text.stroke-79")}),-1.0]])]});
            var Q5;
            Q5=makeQuery(id+"F23.imprint","IMPRINT",FACE,{"disambiguationData":[TD([[makeQuery(id+"F23.imprint","IMPRINT",EDGE,{"derivedFrom":sQuery(id+"F23.wireOp",EDGE,"E112.sketch_text.stroke-94")}),-1.0]])]});
            var Q6;
            Q6=makeQuery(id+"F23.imprint","IMPRINT",FACE,{"disambiguationData":[TD([[makeQuery(id+"F23.imprint","IMPRINT",EDGE,{"derivedFrom":sQuery(id+"F23.wireOp",EDGE,"E112.sketch_text.stroke-114")}),-1.0]])]});
            var Q7;
            Q7=makeQuery(id+"F23.imprint","IMPRINT",FACE,{"disambiguationData":[TD([[makeQuery(id+"F23.imprint","IMPRINT",EDGE,{"derivedFrom":sQuery(id+"F23.wireOp",EDGE,"E112.sketch_text.stroke-139")}),-1.0]])]});
            extrude(context, id + "F24", {"entities" : qUnion([Q0, Q1, Q2, Q3, Q4, Q5, Q6, Q7]), "operationType" : NewBodyOperationType.REMOVE, "oppositeDirection" : true, "depth" : 3 * mm, "offsetDistance" : 25 * mm});
        }
        {
            var Q0;
            Q0=makeQuery(id+"F12.opExtrude","SWEPT_FACE",FACE,{"disambiguationData":[OSD([sQuery(id+"F11.wireOp",EDGE,"E70")])]});
            var sketch = newSketch(context, id + "F25", { "sketchPlane" : qUnion([Q0])});
            skText(sketch, "E113", { "text": "P-90", "fontName": "OpenSans-Regular.ttf"});
            const initialGuessF25  = {"E113": [-0.02964, 0.00203, -0.0192, -0.99982, 0.00701]};
            skSetInitialGuess(sketch, initialGuessF25);
            skSolve(sketch);
        }
        {
            var Q0;
            Q0=makeQuery(id+"F25.imprint","IMPRINT",FACE,{"disambiguationData":[TD([[makeQuery(id+"F25.imprint","IMPRINT",EDGE,{"derivedFrom":sQuery(id+"F25.wireOp",EDGE,"E113.sketch_text.stroke-0")}),1.0]])]});
            extrude(context, id + "F26", {"entities" : qUnion([Q0]), "operationType" : NewBodyOperationType.ADD, "depth" : 0.5 * mm, "offsetDistance" : 25.4 * mm});
        }
        {
            var Q0;
            Q0=makeQuery(id+"F1.opExtrude","SWEPT_FACE",FACE,{"disambiguationData":[OSD([sQuery(id+"F0.wireOp",EDGE,"E24")])]});
            var sketch = newSketch(context, id + "F27", { "sketchPlane" : qUnion([Q0])});
            skLineSegment(sketch, "E114.0", {"start": v(-11.43, 4) * mm, "end": v(-23.16, 4) * mm});
            skLineSegment(sketch, "E115.0", {"start": v(-5.46, 4) * mm, "end": v(-11.4, 4) * mm});
            skLineSegment(sketch, "E116.0.0", {"start": v(-13.13, 2.3) * mm, "end": v(-13.13, 1.7) * mm});
            skArc(sketch, "E116.0.1", {"start": v(-13.13, 1.7) * mm, "mid": v(-12.63, 0.5) * mm, "end": v(-11.43, 0) * mm});
            skLineSegment(sketch, "E116.0.2", {"start": v(-11.43, 0) * mm, "end": v(-11.4, 0) * mm});
            skArc(sketch, "E116.0.3", {"start": v(-11.4, 0) * mm, "mid": v(-10.2, 0.5) * mm, "end": v(-9.7, 1.7) * mm});
            skLineSegment(sketch, "E116.0.4", {"start": v(-9.7, 1.7) * mm, "end": v(-9.7, 2.3) * mm});
            skArc(sketch, "E116.0.5", {"start": v(-9.7, 2.3) * mm, "mid": v(-10.2, 3.5) * mm, "end": v(-11.4, 4) * mm});
            skLineSegment(sketch, "E116.0.6", {"start": v(-11.4, 4) * mm, "end": v(-11.43, 4) * mm});
            skArc(sketch, "E116.0.7", {"start": v(-11.43, 4) * mm, "mid": v(-12.63, 3.5) * mm, "end": v(-13.13, 2.3) * mm});
            skArc(sketch, "E117", {"start": v(-12.13, 4) * mm, "mid": v(-12.86, 3.28) * mm, "end": v(-13.13, 2.3) * mm});
            skLineSegment(sketch, "E118", {"start": v(-11.4, 4) * mm, "end": v(-11.4, 3.06) * mm});
            skArc(sketch, "E119.MirrorCS", {"start": v(-10.68, 4) * mm, "mid": v(-9.97, 3.28) * mm, "end": v(-9.7, 2.3) * mm});
            skLineSegment(sketch, "E120", {"start": v(-12.13, 4) * mm, "end": v(-10.68, 4) * mm});
            skLineSegment(sketch, "E121", {"start": v(-13.13, 2.3) * mm, "end": v(-9.7, 2.3) * mm});
            skSolve(sketch);
        }
        {
            var Q0;
            {var subQ1=sQuery(id+"F27.wireOp",EDGE,"E116.0.5");var subQ4=makeQuery(id+"F27.imprint","IMPRINT",EDGE,{"derivedFrom":subQ1});var subQ5=sQuery(id+"F27.wireOp",EDGE,"E116.0.7");var subQ8=makeQuery(id+"F27.imprint","IMPRINT",EDGE,{"derivedFrom":subQ5});Q0=qUnion([makeQuery(id+"F27.imprint","IMPRINT",FACE,{"disambiguationData":[TD([[makeQuery(id+"F27.imprint","IMPRINT",EDGE,{"derivedFrom":sQuery(id+"F27.wireOp",EDGE,"E116.0.0")}),1.0]])]}),makeQuery(id+"F27.imprint","IMPRINT",FACE,{"disambiguationData":[TD([[subQ4,1.0]])]}),makeQuery(id+"F27.imprint","IMPRINT",FACE,{"disambiguationData":[TD([[subQ8,-1.0]])]}),makeQuery(id+"F27.imprint","IMPRINT",FACE,{"disambiguationData":[TD([[subQ4,-1.0]])]})]);}
            var Q1;
            Q1=makeQuery(id+"F1.opExtrude","SWEPT_FACE",FACE,{"disambiguationData":[OSD([sQuery(id+"F0.wireOp",EDGE,"E26")])]});
            extrude(context, id + "F28", {"entities" : qUnion([Q0]), "operationType" : NewBodyOperationType.ADD, "endBound" : BoundingType.UP_TO_SURFACE, "oppositeDirection" : true, "depth" : 25.4 * mm, "endBoundEntityFace" : qUnion([Q1]), "offsetDistance" : 25.4 * mm});
        }
    });
